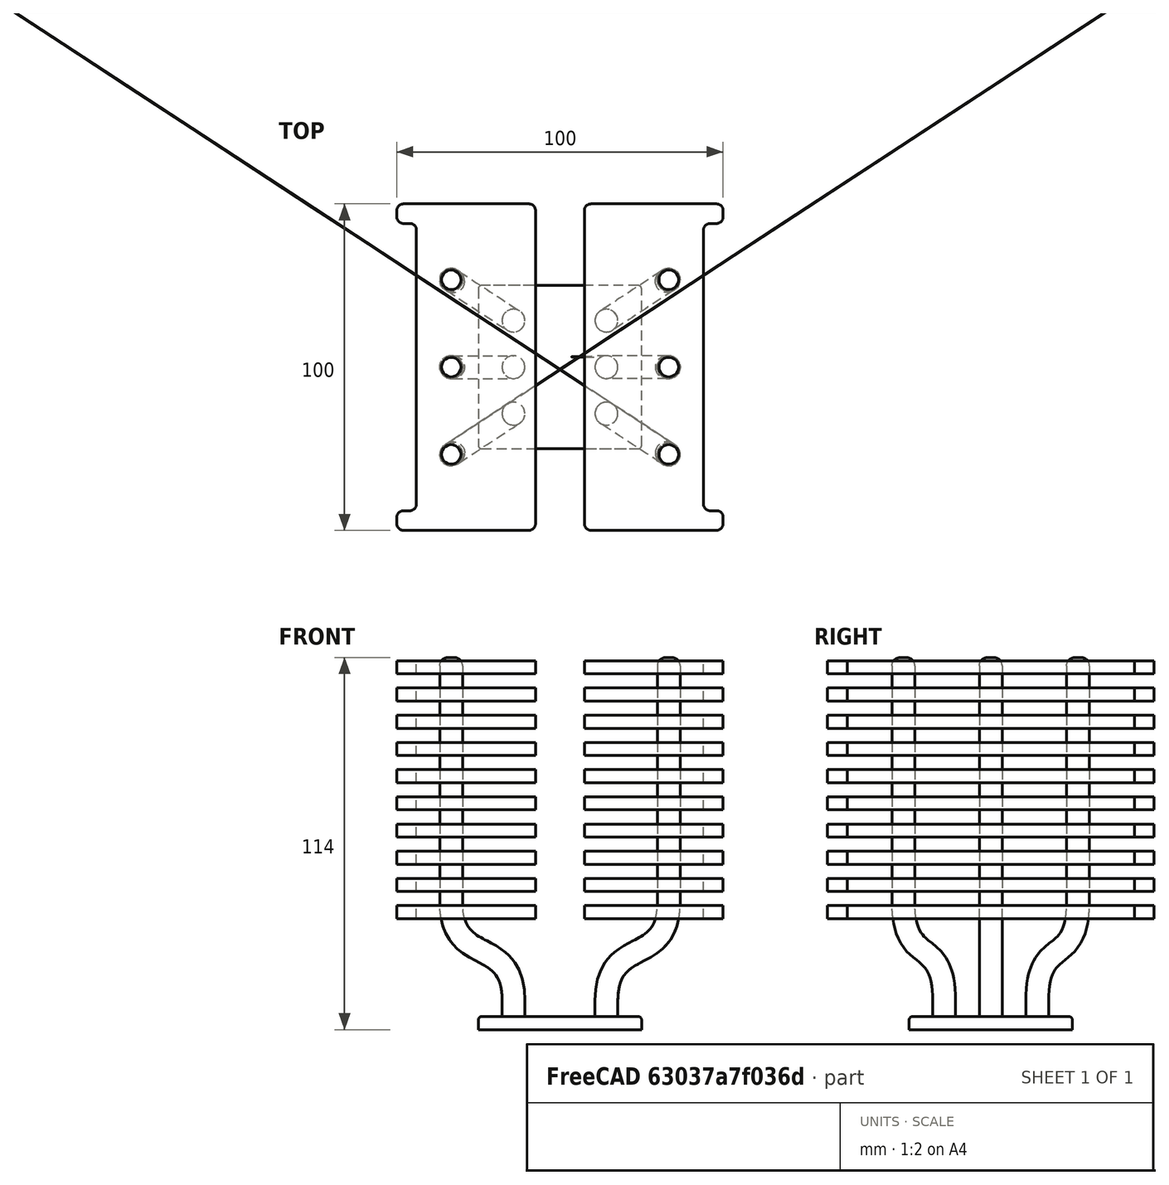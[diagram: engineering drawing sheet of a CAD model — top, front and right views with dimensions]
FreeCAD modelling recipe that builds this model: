
FCSTD DOCUMENT  (FreeCAD 1.0R38642 (Git))
Label: heatsink_small
License: All rights reserved
LicenseURL: https://en.wikipedia.org/wiki/All_rights_reserved
objects: Sketcher::SketchObject×9, Part::Cut×6, PartDesign::SubShapeBinder×5, Part::Mirroring×5, PartDesign::Fillet×4, PartDesign::Body×4, PartDesign::Pad×3, PartDesign::Plane×3, Fem::FeaturePython×3, PartDesign::AdditivePipe×2, Spreadsheet::Sheet×1, PartDesign::LinearPattern×1, Part::FeaturePython×1, Fem::FemMeshShapeBaseObjectPython×1
note: 71 computed .brp shape members not serialized (recipe doc carries the construction recipe); baked Part::Feature solids carry a one-line shape summary decoded from their .brp

FEATURE [Spreadsheet::Sheet] Spreadsheet
  cells = A1='Base Plate; A2='size; B2(base_size)==50 mm; A3='thickness; B3(base_thickness)==4 mm; A4='radius; B4(base_radius)==3 mm; A5='fillet; B5(base_fillet)==1 mm; A7='Pipes; A8='diameter; B8(pipe_diam)==7 mm; A9='distance; B9(pipe_distance)==(base_size - 3 * pipe_diam) / 4; A10='lower height; B10(pipe_lheight)==30 mm; A11='upper distance; B11(pipe_udistance)==(body_size - 3 * pipe_diam) / 4; A12='lower straight; B12(pipe_lstraight)==5 mm; A13='spline param; B13(pipe_splinep)==20 mm; A14='upper height; B14(pipe_uheight)==5 mm; A15='fillet; B15(pipe_fillet)==2.5 mm; A17='Main body; A18='size; B18(body_size)==100 mm; A19='height; B19(body_height)==75 mm; A21='Fins; A22='fillet; B22(fin_fillet)==2 mm; A23='middle space; B23(fin_mspace)==15 mm; A24='dent; B24(fin_dent)==6 mm; A25='thickness; B25(fin_thickness)==4 mm; A26='count; B26(fin_count)=10
FEATURE [Sketcher::SketchObject] Sketch
  ArcFitTolerance = 1e-06
  AttachmentSupport = -> [XY_Plane]
  FullyConstrained = true
  MakeInternals = false
  MapMode = 5
  expr: Constraints[8] = Spreadsheet.base_size
  sketch-geometry (4):
    g0: LineSegment StartX=-25 StartY=25 StartZ=0 EndX=-25 EndY=-25 EndZ=0
    g1: LineSegment StartX=-25 StartY=-25 StartZ=0 EndX=25 EndY=-25 EndZ=0
    g2: LineSegment StartX=25 StartY=-25 StartZ=0 EndX=25 EndY=25 EndZ=0
    g3: LineSegment StartX=25 StartY=25 StartZ=0 EndX=-25 EndY=25 EndZ=0
  constraints (11):
    c: Coincident(g0,g1)
    c: Coincident(g1,g2)
    c: Coincident(g2,g3)
    c: Coincident(g3,g0)
    c: Vertical(g0)
    c: Vertical(g2)
    c: Horizontal(g1)
    c: Horizontal(g3)
    c: DistanceY(g0,g0) = 50
    c: Equal(g0,g3)
    c: Symmetric(g0,g1,g-1)
FEATURE [PartDesign::Pad] Pad
  Direction = (0,0,1)
  Length = 4
  Length2 = 10
  Profile = -> Sketch
  ReferenceAxis = -> Sketch [N_Axis]
  Refine = true
  Reversed = true
  Suppressed = false
  Type = 0
  expr: Length = Spreadsheet.base_thickness
FEATURE [PartDesign::Fillet] Fillet
  Base = -> Pad [Edge5,Edge8,Edge1,Edge2]
  BaseFeature = -> Pad
  Radius = 3
  Refine = true
  SupportTransform = false
  Suppressed = false
  UseAllEdges = false
  expr: Radius = Spreadsheet.base_radius
FEATURE [Sketcher::SketchObject] Sketch001  label="PipeCenters"
  ArcFitTolerance = 1e-06
  AttachmentSupport = -> [XY_Plane001]
  FullyConstrained = true
  MakeInternals = false
  MapMode = 5
  expr: Constraints[11] = Spreadsheet.pipe_distance + Spreadsheet.pipe_diam / 2
  expr: Constraints[12] = Spreadsheet.pipe_distance + Spreadsheet.pipe_diam / 2
  expr: Constraints[14] = Spreadsheet.pipe_distance + Spreadsheet.pipe_diam
  expr: Constraints[16] = Spreadsheet.pipe_distance + Spreadsheet.pipe_diam
  expr: Constraints[9] = Spreadsheet.base_size
  sketch-geometry (7):
    g0: LineSegment [constr] StartX=-25 StartY=25 StartZ=0 EndX=-25 EndY=-25 EndZ=0
    g1: LineSegment [constr] StartX=-25 StartY=-25 StartZ=0 EndX=25 EndY=-25 EndZ=0
    g2: LineSegment [constr] StartX=25 StartY=-25 StartZ=0 EndX=25 EndY=25 EndZ=0
    g3: LineSegment [constr] StartX=25 StartY=25 StartZ=0 EndX=-25 EndY=25 EndZ=0
    g4: GeomPoint X=-14.25 Y=-14.25 Z=0
    g5: GeomPoint X=-14.25 Y=-1e-15 Z=0
    g6: GeomPoint X=-14.25 Y=14.25 Z=0
  constraints (17):
    c: Coincident(g0,g1)
    c: Coincident(g1,g2)
    c: Coincident(g2,g3)
    c: Coincident(g3,g0)
    c: Vertical(g0)
    c: Vertical(g2)
    c: Horizontal(g1)
    c: Horizontal(g3)
    c: Symmetric(g0,g1,g-1)
    c: DistanceY(g0,g0) = 50
    c: Equal(g2,g3)
    c: DistanceX(g0,g4) = 10.75
    c: DistanceY(g0,g4) = 10.75
    c: Vertical(g5,g4)
    c: DistanceY(g4,g5) = 14.25
    c: Vertical(g5,g6)
    c: DistanceY(g5,g6) = 14.25
FEATURE [PartDesign::SubShapeBinder] Binder  label="LowerEnd"
  BindCopyOnChange = 0
  BindMode = 0
  ClaimChildren = false
  Context = -> Body001 [Binder.]
  Fuse = false
  MakeFace = true
  OffsetFill = false
  OffsetIntersection = false
  OffsetJoinType = 0
  OffsetOpenResult = false
  PartialLoad = false
  Refine = true
  Relative = true
  Support = -> [Sketch001[Vertex1]]
  _Version = 2
FEATURE [Sketcher::SketchObject] Sketch002  label="BaseShape"
  ArcFitTolerance = 1e-06
  AttachmentSupport = -> [XY_Plane001]
  ExternalGeometry = -> [Binder]
  FullyConstrained = true
  MakeInternals = false
  MapMode = 5
  expr: Constraints[1] = Spreadsheet.pipe_diam
  sketch-geometry (1):
    g0: Circle CenterX=-14.25 CenterY=-14.25 CenterZ=0 NormalX=0 NormalY=0 NormalZ=1 AngleXU=0 Radius=3.5
  constraints (2):
    c: Coincident(g0,g-3)
    c: Diameter(g0) = 7
FEATURE [PartDesign::SubShapeBinder] Binder001  label="LowerEnd001"
  BindCopyOnChange = 0
  BindMode = 0
  ClaimChildren = false
  Context = -> Body002 [Binder001.]
  Fuse = false
  MakeFace = true
  OffsetFill = false
  OffsetIntersection = false
  OffsetJoinType = 0
  OffsetOpenResult = false
  PartialLoad = false
  Refine = true
  Relative = true
  Support = -> [Sketch001[Vertex2]]
  _Version = 2
FEATURE [Sketcher::SketchObject] Sketch003  label="BaseShape001"
  ArcFitTolerance = 1e-06
  AttachmentSupport = -> [XY_Plane002]
  ExternalGeometry = -> [Binder001]
  FullyConstrained = true
  MakeInternals = false
  MapMode = 5
  expr: Constraints[1] = Spreadsheet.pipe_diam
  sketch-geometry (1):
    g0: Circle CenterX=-14.25 CenterY=0 CenterZ=0 NormalX=0 NormalY=0 NormalZ=1 AngleXU=0 Radius=3.5
  constraints (2):
    c: Coincident(g0,g-3)
    c: Diameter(g0) = 7
FEATURE [PartDesign::Plane] DatumPlane
  AttachmentOffset = pos=(0,0,30) rot=(0,0,1;0rad)
  AttachmentSupport = -> [XY_Plane]
  Length = 60
  MapMode = 5
  Placement = pos=(0,0,30) rot=(0,0,1;0rad)
  ResizeMode = 0
  Width = 60
  expr: .AttachmentOffset.Base.z = Spreadsheet.pipe_lheight
FEATURE [Sketcher::SketchObject] Sketch006  label="PipeCentersTop"
  ArcFitTolerance = 1e-06
  AttachmentSupport = -> [DatumPlane]
  FullyConstrained = true
  MakeInternals = false
  MapMode = 5
  Placement = pos=(0,0,30) rot=(0,0,1;0rad)
  expr: Constraints[13] = Spreadsheet.pipe_udistance + Spreadsheet.pipe_diam / 2
  expr: Constraints[14] = Spreadsheet.pipe_udistance / 1.5 + Spreadsheet.pipe_diam / 2
  expr: Constraints[15] = Spreadsheet.pipe_udistance + Spreadsheet.pipe_diam
  expr: Constraints[16] = Spreadsheet.pipe_udistance + Spreadsheet.pipe_diam
  expr: Constraints[8] = Spreadsheet.body_size
  sketch-geometry (7):
    g0: LineSegment StartX=-50 StartY=50 StartZ=0 EndX=-50 EndY=-50 EndZ=0
    g1: LineSegment StartX=-50 StartY=-50 StartZ=0 EndX=50 EndY=-50 EndZ=0
    g2: LineSegment StartX=50 StartY=-50 StartZ=0 EndX=50 EndY=50 EndZ=0
    g3: LineSegment StartX=50 StartY=50 StartZ=0 EndX=-50 EndY=50 EndZ=0
    g4: GeomPoint X=-33.3333 Y=-26.75 Z=0
    g5: GeomPoint X=-33.3333 Y=-5e-16 Z=0
    g6: GeomPoint X=-33.3333 Y=26.75 Z=0
  constraints (17):
    c: Coincident(g0,g1)
    c: Coincident(g1,g2)
    c: Coincident(g2,g3)
    c: Coincident(g3,g0)
    c: Vertical(g0)
    c: Vertical(g2)
    c: Horizontal(g1)
    c: Horizontal(g3)
    c: DistanceX(g3,g3) = 100
    c: Equal(g0,g3)
    c: Symmetric(g0,g1,g-1)
    c: Vertical(g6,g5)
    c: Vertical(g5,g4)
    c: DistanceY(g0,g4) = 23.25
    c: DistanceX(g0,g4) = 16.6667
    c: DistanceY(g4,g5) = 26.75
    c: DistanceY(g5,g6) = 26.75
FEATURE [PartDesign::SubShapeBinder] Binder003  label="UpperEnd"
  BindCopyOnChange = 0
  BindMode = 0
  ClaimChildren = false
  Context = -> Body001 [Binder003.]
  Fuse = false
  MakeFace = true
  OffsetFill = false
  OffsetIntersection = false
  OffsetJoinType = 0
  OffsetOpenResult = false
  PartialLoad = false
  Refine = true
  Relative = true
  Support = -> [Body[Sketch006.Vertex5]]
  _Version = 2
FEATURE [PartDesign::Plane] DatumPlane001
  AttachmentSupport = -> [Binder,Z_Axis001,Binder003]
  Length = 103.037
  MapMode = 52
  Placement = pos=(-14.25,-14.25,0) rot=(-0.206426,0.691877,0.691877;3.54873rad)
  ResizeMode = 0
  Width = 156.042
FEATURE [Sketcher::SketchObject] Sketch007  label="Path"
  ArcFitTolerance = 1e-06
  AttachmentSupport = -> [DatumPlane001]
  ExternalGeometry = -> [Binder003]
  FullyConstrained = true
  MakeInternals = false
  MapMode = 5
  Placement = pos=(-14.25,-14.25,0) rot=(-0.206426,0.691877,0.691877;3.54873rad)
  expr: Constraints[19] = Spreadsheet.pipe_splinep
  expr: Constraints[20] = Spreadsheet.pipe_splinep
  expr: Constraints[23] = Spreadsheet.body_height + Spreadsheet.pipe_uheight
  expr: Constraints[4] = Spreadsheet.pipe_lstraight
  sketch-geometry (10):
    g0: LineSegment StartX=0 StartY=0 StartZ=0 EndX=0 EndY=5 EndZ=0
    g1: LineSegment StartX=22.8128 StartY=30 StartZ=0 EndX=22.8128 EndY=35 EndZ=0
    g2-g5: Circle [constr] x4 (B-spline internal-alignment scaffolding for g6; pole/knot coordinates omitted)
    g6: BSplineCurve PolesCount=4 KnotsCount=2 Degree=3 IsPeriodic=0
    g7: GeomPoint [constr] X=0 Y=5 Z=0
    g8: GeomPoint [constr] X=22.8128 Y=35 Z=0
    g9: LineSegment StartX=22.8128 StartY=30 StartZ=0 EndX=22.8128 EndY=110 EndZ=0
  constraints (22):
    c: Coincident(g0,g-1)
    c: PointOnObject(g0,g-2)
    c: Coincident(g1,g-3)
    c: Vertical(g1)
    c: DistanceY(g0,g0) = 5
    c: Weight(g2) = 1
    c: Equal(g2,g3)
    c: Equal(g2,g4)
    c: Equal(g2,g5)
    c: InternalAlignment(g2-g5 -> g6) x4
    c: InternalAlignment(g7,g6)
    c: InternalAlignment(g8,g6)
    c: Coincident(g2,g0)
    c: Coincident(g5,g1)
    c: PointOnObject(g3,g-2)
    c: Vertical(g4,g6)
    c: DistanceY(g4,g6) = 20
    c: DistanceY(g6,g3) = 20
    c: Coincident(g9,g1)
    c: Vertical(g9)
    c: DistanceY(g9,g9) = 80
    c: Equal(g1,g0)
FEATURE [PartDesign::AdditivePipe] AdditivePipe
  AuxilleryCurvelinear = true
  AuxillerySpineTangent = false
  Binormal = (0,0,0)
  Mode = 0
  Profile = -> Sketch002
  Refine = true
  Spine = -> Sketch007
  SpineTangent = false
  Suppressed = false
  Transformation = 0
  Transition = 0
FEATURE [PartDesign::SubShapeBinder] Binder004  label="UpperEnd001"
  BindCopyOnChange = 0
  BindMode = 0
  ClaimChildren = false
  Context = -> Body002 [Binder004.]
  Fuse = false
  MakeFace = true
  OffsetFill = false
  OffsetIntersection = false
  OffsetJoinType = 0
  OffsetOpenResult = false
  PartialLoad = false
  Refine = true
  Relative = true
  Support = -> [Body[Sketch006.Vertex6]]
  _Version = 2
FEATURE [PartDesign::Plane] DatumPlane002
  AttachmentSupport = -> [Binder001,Z_Axis002,Binder004]
  Length = 80.1063
  MapMode = 52
  Placement = pos=(-14.25,-1e-15,0) rot=(0,0.707107,0.707107;3.14159rad)
  ResizeMode = 0
  Width = 153.273
FEATURE [Sketcher::SketchObject] Sketch008  label="Path001"
  ArcFitTolerance = 1e-06
  AttachmentSupport = -> [DatumPlane002]
  ExternalGeometry = -> [Binder004]
  FullyConstrained = true
  MakeInternals = false
  MapMode = 5
  Placement = pos=(-14.25,-1e-15,0) rot=(0,0.707107,0.707107;3.14159rad)
  expr: Constraints[20] = Spreadsheet.pipe_splinep
  expr: Constraints[21] = Spreadsheet.pipe_splinep
  expr: Constraints[24] = Spreadsheet.body_height + Spreadsheet.pipe_uheight
  expr: Constraints[4] = Spreadsheet.pipe_lstraight
  sketch-geometry (10):
    g0: LineSegment StartX=0 StartY=0 StartZ=0 EndX=0 EndY=5 EndZ=0
    g1: LineSegment StartX=19.0833 StartY=30 StartZ=0 EndX=19.0833 EndY=35 EndZ=0
    g2-g5: Circle [constr] x4 (B-spline internal-alignment scaffolding for g6; pole/knot coordinates omitted)
    g6: BSplineCurve PolesCount=4 KnotsCount=2 Degree=3 IsPeriodic=0
    g7: GeomPoint [constr] X=0 Y=5 Z=0
    g8: GeomPoint [constr] X=19.0833 Y=35 Z=0
    g9: LineSegment StartX=19.0833 StartY=30 StartZ=0 EndX=19.0833 EndY=110 EndZ=0
  constraints (22):
    c: Coincident(g0,g-1)
    c: Vertical(g0)
    c: Coincident(g1,g-3)
    c: Vertical(g1)
    c: DistanceY(g0,g0) = 5
    c: Equal(g1,g0)
    c: Weight(g2) = 1
    c: Equal(g2,g3)
    c: Equal(g2,g4)
    c: Equal(g2,g5)
    c: InternalAlignment(g2-g5 -> g6) x4
    c: InternalAlignment(g7,g6)
    c: InternalAlignment(g8,g6)
    c: Coincident(g2,g0)
    c: Coincident(g5,g1)
    c: Vertical(g4,g6)
    c: PointOnObject(g3,g-2)
    c: DistanceY(g6,g3) = 20
    c: DistanceY(g4,g6) = 20
    c: Coincident(g9,g1)
    c: Vertical(g9)
    c: DistanceY(g9,g9) = 80
FEATURE [PartDesign::AdditivePipe] AdditivePipe001
  AuxilleryCurvelinear = true
  AuxillerySpineTangent = false
  Binormal = (0,0,0)
  Mode = 0
  Profile = -> Sketch003
  Refine = true
  Spine = -> Sketch008
  SpineTangent = false
  Suppressed = false
  Transformation = 0
  Transition = 0
FEATURE [PartDesign::Fillet] Fillet001
  Base = -> AdditivePipe [Edge7]
  BaseFeature = -> AdditivePipe
  Radius = 2.5
  Refine = true
  SupportTransform = false
  Suppressed = false
  UseAllEdges = false
  expr: Radius = Spreadsheet.pipe_fillet
FEATURE [PartDesign::Body] Body001  label="CornerPipe"
  AllowCompound = false
  Group = -> [Binder,Sketch002,Binder003,DatumPlane001,Sketch007,AdditivePipe,Fillet001]
  Origin = -> Origin001
  Tip = -> Fillet001
FEATURE [Part::Mirroring] Part__Mirroring  label="CornerPipe (Mirror #1)"
  Base = (0,0,0)
  Normal = (0,1,0)
  Source = -> Body001
FEATURE [Part::Mirroring] Part__Mirroring001  label="CornerPipe (Mirror #2)"
  Base = (0,0,0)
  Normal = (1,0,0)
  Source = -> Body001
FEATURE [Part::Mirroring] Part__Mirroring002  label="CornerPipe (Mirror #3)"
  Base = (0,0,0)
  Normal = (0,1,0)
  Source = -> Part__Mirroring001
FEATURE [PartDesign::Fillet] Fillet002
  Base = -> AdditivePipe001 [Edge7]
  BaseFeature = -> AdditivePipe001
  Radius = 2.5
  Refine = true
  SupportTransform = false
  Suppressed = false
  UseAllEdges = false
  expr: Radius = Spreadsheet.pipe_fillet
FEATURE [PartDesign::Body] Body002  label="MiddlePipe"
  AllowCompound = false
  Group = -> [Binder001,Sketch003,Binder004,DatumPlane002,Sketch008,AdditivePipe001,Fillet002]
  Origin = -> Origin002
  Tip = -> Fillet002
FEATURE [Part::Mirroring] Part__Mirroring003  label="MiddlePipe (Mirror #1)"
  Base = (0,0,0)
  Normal = (1,0,0)
  Source = -> Body002
FEATURE [PartDesign::Fillet] Fillet003
  Base = -> Pad [Edge6,Edge3,Edge11,Edge9,Edge5,Edge2,Edge8,Edge1]
  BaseFeature = -> Pad
  Radius = 1
  Refine = true
  SupportTransform = false
  Suppressed = false
  UseAllEdges = false
  expr: Radius = Spreadsheet.base_fillet
FEATURE [PartDesign::Body] Body  label="Base"
  AllowCompound = false
  Group = -> [Sketch,Pad,Fillet,DatumPlane,Sketch006,Fillet003]
  Origin = -> Origin
  Tip = -> Fillet003
FEATURE [Sketcher::SketchObject] Sketch009
  ArcFitTolerance = 1e-06
  AttachmentSupport = -> [XY_Plane003]
  FullyConstrained = true
  MakeInternals = false
  MapMode = 5
  expr: Constraints[10] = Spreadsheet.body_size
  expr: Constraints[59] = Spreadsheet.fin_fillet
  expr: Constraints[61] = Spreadsheet.fin_mspace / 2
  expr: Constraints[62] = Spreadsheet.fin_dent
  expr: Constraints[63] = Spreadsheet.fin_dent
  sketch-geometry (28):
    g0: LineSegment [constr] StartX=-50 StartY=50 StartZ=0 EndX=-50 EndY=-50 EndZ=0
    g1: LineSegment [constr] StartX=-50 StartY=-50 StartZ=0 EndX=50 EndY=-50 EndZ=0
    g2: LineSegment [constr] StartX=50 StartY=-50 StartZ=0 EndX=50 EndY=50 EndZ=0
    g3: LineSegment [constr] StartX=50 StartY=50 StartZ=0 EndX=-50 EndY=50 EndZ=0
    g4: LineSegment StartX=-9.5 StartY=50 StartZ=0 EndX=-48 EndY=50 EndZ=0
    g5: LineSegment StartX=-50 StartY=48 StartZ=0 EndX=-50 EndY=46 EndZ=0
    g6: LineSegment StartX=-48 StartY=44 StartZ=0 EndX=-46 EndY=44 EndZ=0
    g7: LineSegment StartX=-44 StartY=42 StartZ=0 EndX=-44 EndY=-42 EndZ=0
    g8: LineSegment StartX=-46 StartY=-44 StartZ=0 EndX=-48 EndY=-44 EndZ=0
    g9: LineSegment StartX=-50 StartY=-46 StartZ=0 EndX=-50 EndY=-48 EndZ=0
    g10: LineSegment StartX=-48 StartY=-50 StartZ=0 EndX=-9.5 EndY=-50 EndZ=0
    g11: LineSegment StartX=-7.5 StartY=-48 StartZ=0 EndX=-7.5 EndY=48 EndZ=0
    g12: ArcOfCircle CenterX=-48 CenterY=-48 CenterZ=0 NormalX=0 NormalY=0 NormalZ=1 AngleXU=0 Radius=2 StartAngle=3.14159 EndAngle=4.71239
    g13: GeomPoint [constr] X=-50 Y=-50 Z=0
    g14: ArcOfCircle CenterX=-48 CenterY=-46 CenterZ=0 NormalX=0 NormalY=0 NormalZ=1 AngleXU=0 Radius=2 StartAngle=1.5708 EndAngle=3.14159
    g15: GeomPoint [constr] X=-50 Y=-44 Z=0
    g16: ArcOfCircle CenterX=-46 CenterY=-42 CenterZ=0 NormalX=0 NormalY=0 NormalZ=1 AngleXU=0 Radius=2 StartAngle=4.71239 EndAngle=6.28319
    g17: GeomPoint [constr] X=-44 Y=-44 Z=0
    g18: ArcOfCircle CenterX=-46 CenterY=42 CenterZ=0 NormalX=0 NormalY=0 NormalZ=1 AngleXU=0 Radius=2 StartAngle=-9e-16 EndAngle=1.5708
    g19: GeomPoint [constr] X=-44 Y=44 Z=0
    g20: ArcOfCircle CenterX=-48 CenterY=46 CenterZ=0 NormalX=0 NormalY=0 NormalZ=1 AngleXU=0 Radius=2 StartAngle=3.14159 EndAngle=4.71239
    g21: GeomPoint [constr] X=-50 Y=44 Z=0
    g22: ArcOfCircle CenterX=-48 CenterY=48 CenterZ=0 NormalX=0 NormalY=0 NormalZ=1 AngleXU=0 Radius=2 StartAngle=1.5708 EndAngle=3.14159
    g23: GeomPoint [constr] X=-50 Y=50 Z=0
    g24: ArcOfCircle CenterX=-9.5 CenterY=48 CenterZ=0 NormalX=0 NormalY=0 NormalZ=1 AngleXU=0 Radius=2 StartAngle=-3.6e-15 EndAngle=1.5708
    g25: GeomPoint [constr] X=-7.5 Y=50 Z=0
    g26: ArcOfCircle CenterX=-9.5 CenterY=-48 CenterZ=0 NormalX=0 NormalY=0 NormalZ=1 AngleXU=0 Radius=2 StartAngle=4.71239 EndAngle=6.28319
    g27: GeomPoint [constr] X=-7.5 Y=-50 Z=0
  constraints (64):
    c: Coincident(g0,g1)
    c: Coincident(g1,g2)
    c: Coincident(g2,g3)
    c: Coincident(g3,g0)
    c: Vertical(g0)
    c: Vertical(g2)
    c: Horizontal(g1)
    c: Horizontal(g3)
    c: Equal(g0,g3)
    c: Symmetric(g0,g1,g-1)
    c: DistanceX(g1,g1) = 100
    c: PointOnObject(g25,g3)
    c: Coincident(g23,g0)
    c: PointOnObject(g21,g0)
    c: Horizontal(g6)
    c: Vertical(g7)
    c: PointOnObject(g15,g0)
    c: Horizontal(g8)
    c: Coincident(g13,g0)
    c: PointOnObject(g27,g1)
    c: Vertical(g11)
    c: PointOnObject(g13,g10)
    c: PointOnObject(g13,g9)
    c: Tangent(g10,g12) = -1.5708
    c: Tangent(g9,g12) = -1.5708
    c: PointOnObject(g15,g9)
    c: PointOnObject(g15,g8)
    c: Tangent(g9,g14) = -1.5708
    c: Tangent(g8,g14) = -1.5708
    c: PointOnObject(g17,g8)
    c: PointOnObject(g17,g7)
    c: Tangent(g8,g16) = 1.5708
    c: Tangent(g7,g16) = 1.5708
    c: PointOnObject(g19,g6)
    c: Tangent(g7,g18) = 1.5708
    c: Tangent(g6,g18) = 1.5708
    c: PointOnObject(g21,g6)
    c: PointOnObject(g21,g5)
    c: Tangent(g6,g20) = -1.5708
    c: Tangent(g5,g20) = -1.5708
    c: PointOnObject(g23,g5)
    c: PointOnObject(g23,g4)
    c: Tangent(g5,g22) = -1.5708
    c: Tangent(g4,g22) = -1.5708
    c: PointOnObject(g25,g4)
    c: PointOnObject(g25,g11)
    c: Tangent(g4,g24) = -1.5708
    c: Tangent(g11,g24) = -1.5708
    c: PointOnObject(g27,g11)
    c: PointOnObject(g27,g10)
    c: Tangent(g11,g26) = -1.5708
    c: Tangent(g10,g26) = -1.5708
    c: Equal(g24,g22)
    c: Equal(g22,g20)
    c: Equal(g20,g18)
    c: Equal(g18,g26)
    c: Equal(g26,g12)
    c: Equal(g12,g14)
    c: Equal(g14,g16)
    c: Radius(g26) = 2
    c: Symmetric(g17,g19,g-1)
    c: DistanceX(g11,g-1) = 7.5
    c: DistanceX(g0,g17) = 6
    c: DistanceY(g0,g15) = 6
FEATURE [PartDesign::SubShapeBinder] Binder005
  BindCopyOnChange = 0
  BindMode = 0
  ClaimChildren = false
  Context = -> Body003 [Binder005.]
  Fuse = false
  MakeFace = true
  OffsetFill = false
  OffsetIntersection = false
  OffsetJoinType = 0
  OffsetOpenResult = false
  PartialLoad = false
  Refine = true
  Relative = true
  Support = -> [Body[Sketch006.Vertex6]]
  _Version = 2
FEATURE [Sketcher::SketchObject] Sketch010
  ArcFitTolerance = 1e-06
  AttachmentSupport = -> [XY_Plane003]
  ExternalGeometry = -> [Binder005]
  FullyConstrained = true
  MakeInternals = false
  MapMode = 5
  expr: Constraints[1] = Spreadsheet.pipe_diam / 2
  sketch-geometry (1):
    g0: Circle CenterX=-33.3333 CenterY=0 CenterZ=0 NormalX=0 NormalY=0 NormalZ=1 AngleXU=0 Radius=1.75
  constraints (2):
    c: Coincident(g0,g-3)
    c: Diameter(g0) = 3.5
FEATURE [PartDesign::Pad] Pad002
  Direction = (0,0,1)
  Length = 75
  Length2 = 10
  Profile = -> Sketch010
  ReferenceAxis = -> Sketch010 [N_Axis]
  Refine = true
  Suppressed = false
  Type = 0
  expr: Length = Spreadsheet.body_height
FEATURE [PartDesign::Pad] Pad001
  BaseFeature = -> Pad002
  Direction = (0,0,1)
  Length = 4
  Length2 = 10
  Profile = -> Sketch009
  ReferenceAxis = -> Sketch009 [N_Axis]
  Refine = true
  Suppressed = false
  Type = 0
  expr: Length = Spreadsheet.fin_thickness
FEATURE [PartDesign::LinearPattern] LinearPattern
  BaseFeature = -> Pad001
  Direction = -> Sketch009 [N_Axis]
  Length = 75
  Mode = 0
  Occurrences = 10
  Offset = 8.33333
  Originals = -> [Pad001]
  Refine = true
  Suppressed = false
  TransformMode = 0
  expr: Length = Spreadsheet.body_height
  expr: Occurrences = Spreadsheet.fin_count
FEATURE [PartDesign::Body] Body003  label="Fins"
  AllowCompound = false
  Group = -> [Sketch009,Binder005,Sketch010,Pad002,Pad001,LinearPattern]
  Origin = -> Origin003
  Placement = pos=(0,0,30) rot=(0,0,1;0rad)
  Tip = -> LinearPattern
  expr: .Placement.Base.z = Spreadsheet.pipe_lheight
FEATURE [Part::Mirroring] Part__Mirroring004  label="Fins (Mirror #5)"
  Base = (0,0,0)
  Normal = (1,0,0)
  Source = -> Body003
FEATURE [Part::Cut] Cut
  Base = -> Body003
  Refine = true
  Tool = -> Body001
FEATURE [Part::Cut] Cut001
  Base = -> Cut
  Refine = true
  Tool = -> Part__Mirroring
FEATURE [Part::Cut] Cut002  label="CutFins"
  Base = -> Cut001
  Refine = true
  Tool = -> Body002
FEATURE [Part::Cut] Cut003
  Base = -> Part__Mirroring004
  Refine = true
  Tool = -> Part__Mirroring002
FEATURE [Part::Cut] Cut004
  Base = -> Cut003
  Refine = true
  Tool = -> Part__Mirroring001
FEATURE [Part::Cut] Cut005  label="CutFins Mirror"
  Base = -> Cut004
  Refine = true
  Tool = -> Part__Mirroring003
FEATURE [Part::FeaturePython] BooleanFragments  # WARN: FeaturePython — macro-defined, semantics opaque (R4)
  Mode = 0
  Objects = -> [Cut002,Cut005,Body001,Part__Mirroring001,Part__Mirroring002,Part__Mirroring003,Part__Mirroring,Body002,Body]
  Tolerance = 0
FEATURE [Fem::FeaturePython] MeshGroup  label="BaseBody"  # FEM object (typed FeaturePython)
  References = -> [BooleanFragments]
  UseLabel = true
FEATURE [Fem::FeaturePython] MeshGroup001  label="Pipes"  # FEM object (typed FeaturePython)
  References = -> [BooleanFragments]
  UseLabel = true
FEATURE [Fem::FeaturePython] MeshGroup002  label="Bottom"  # FEM object (typed FeaturePython)
  References = -> [BooleanFragments]
  UseLabel = true
FEATURE [Fem::FemMeshShapeBaseObjectPython] FEMMeshGmsh  # FEM object (typed FeaturePython)
  Algorithm2D = 1
  Algorithm3D = 1
  CharacteristicLengthMax = 0
  CharacteristicLengthMin = 0
  CoherenceMesh = true
  ElementDimension = 3
  ElementOrder = 0
  GeometryTolerance = 1e-06
  GroupsOfNodes = false
  HighOrderOptimize = 0
  MeshGroupList = -> [MeshGroup,MeshGroup001,MeshGroup002]
  MeshSizeFromCurvature = 12
  OptimizeNetgen = false
  OptimizeStd = true
  RecombinationAlgorithm = 0
  Recombine3DAll = false
  RecombineAll = false
  SecondOrderLinear = false
  Shape = -> BooleanFragments
  SubdivisionAlgorithm = 0
